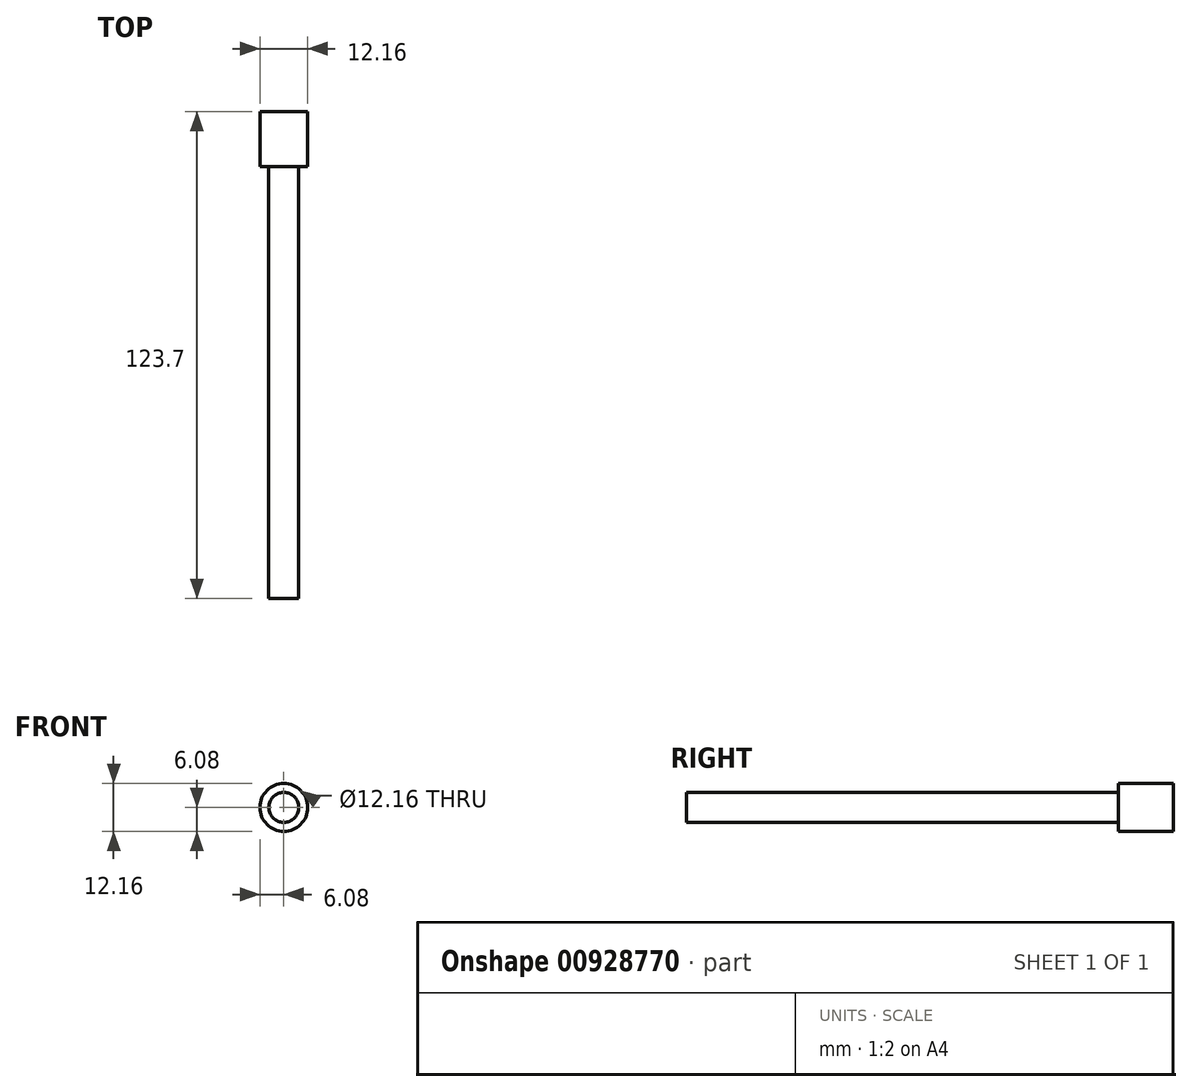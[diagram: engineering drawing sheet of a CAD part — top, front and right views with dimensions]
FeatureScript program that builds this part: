
annotation { "Feature Type Name" : "Feature", "Feature Type Description" : "" }
export const myFeature = defineFeature(function(context is Context, id is Id, definition is map)
    precondition{}
    {
        {
            var Q0;
            Q0=qCreatedBy(makeId("Front.planeOp"),FACE);
            var sketch = newSketch(context, id + "F0", { "sketchPlane" : qUnion([Q0])});
            skCircle(sketch, "E0", {"center": v(0, 0) * mm, "radius": 3.81 * mm});
            skSolve(sketch);
        }
        {
            var Q0;
            Q0=sQuery(id+"F0.wireOp",EDGE,"E0");
            extrude(context, id + "F1", {"bodyType" : ToolBodyType.SURFACE, "surfaceEntities" : qUnion([Q0]), "depth" : 109.73 * mm, "offsetDistance" : 25.4 * mm});
        }
        {
            var Q0;
            Q0=qCreatedBy(makeId("Front.planeOp"),FACE);
            var sketch = newSketch(context, id + "F2", { "sketchPlane" : qUnion([Q0])});
            skCircle(sketch, "E1", {"center": v(0, 0) * mm, "radius": 6.08 * mm});
            skCircle(sketch, "E2", {"center": v(0, 0) * mm, "radius": 11.05 * mm});
            skSolve(sketch);
        }
        {
            var Q0;
            Q0=sQuery(id+"F2.wireOp",EDGE,"E1");
            extrude(context, id + "F3", {"bodyType" : ToolBodyType.SURFACE, "surfaceEntities" : qUnion([Q0]), "oppositeDirection" : true, "depth" : 13.97 * mm, "offsetDistance" : 25.4 * mm});
        }
    });
